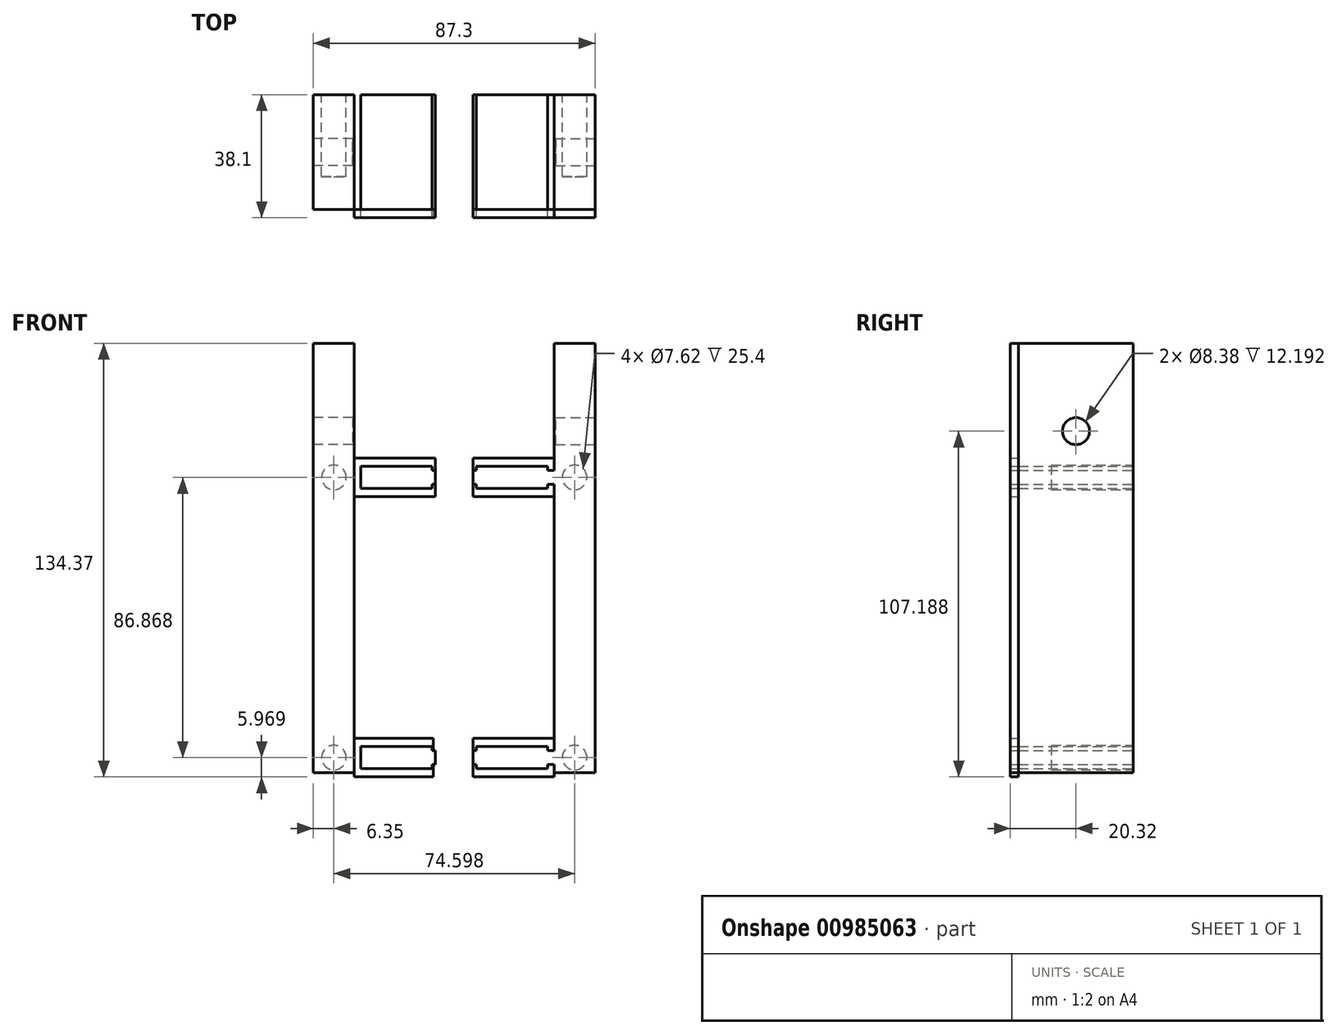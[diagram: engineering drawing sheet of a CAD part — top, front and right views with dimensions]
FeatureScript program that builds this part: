
annotation { "Feature Type Name" : "Feature", "Feature Type Description" : "" }
export const myFeature = defineFeature(function(context is Context, id is Id, definition is map)
    precondition{}
    {
        {
            var Q0;
            Q0=qCreatedBy(makeId("Front.planeOp"),FACE);
            var sketch = newSketch(context, id + "F0", { "sketchPlane" : qUnion([Q0])});
            skLineSegment(sketch, "E0.bottom", {"start": v(-12.7, 133.1) * mm, "end": v(0, 133.1) * mm});
            skLineSegment(sketch, "E0.top", {"start": v(-12.7, 0) * mm, "end": v(0, 0) * mm});
            skLineSegment(sketch, "E0.left", {"start": v(-12.7, 133.1) * mm, "end": v(-12.7, 0) * mm});
            skLineSegment(sketch, "E0.right", {"start": v(0, 133.1) * mm, "end": v(0, 0) * mm});
            skLineSegment(sketch, "E1.bottom", {"start": v(0, 6.86) * mm, "end": v(25.15, 6.86) * mm});
            skLineSegment(sketch, "E1.top", {"start": v(0, 2.54) * mm, "end": v(25.15, 2.54) * mm});
            skLineSegment(sketch, "E1.left", {"start": v(0, 6.86) * mm, "end": v(0, 2.54) * mm});
            skLineSegment(sketch, "E1.right", {"start": v(25.15, 6.86) * mm, "end": v(25.15, 2.54) * mm});
            skLineSegment(sketch, "E2.bottom", {"start": v(2.03, 8.13) * mm, "end": v(24.13, 8.13) * mm});
            skLineSegment(sketch, "E2.top", {"start": v(2.03, 1.27) * mm, "end": v(24.13, 1.27) * mm});
            skLineSegment(sketch, "E2.left", {"start": v(2.03, 8.13) * mm, "end": v(2.03, 1.27) * mm});
            skLineSegment(sketch, "E2.right", {"start": v(24.13, 8.13) * mm, "end": v(24.13, 1.27) * mm});
            skLineSegment(sketch, "E3.bottom", {"start": v(0, 93.73) * mm, "end": v(25.15, 93.73) * mm});
            skLineSegment(sketch, "E3.top", {"start": v(0, 89.4) * mm, "end": v(25.15, 89.4) * mm});
            skLineSegment(sketch, "E3.left", {"start": v(0, 93.73) * mm, "end": v(0, 89.4) * mm});
            skLineSegment(sketch, "E3.right", {"start": v(25.15, 93.73) * mm, "end": v(25.15, 89.4) * mm});
            skLineSegment(sketch, "E4.bottom", {"start": v(2.03, 95) * mm, "end": v(24.13, 95) * mm});
            skLineSegment(sketch, "E4.top", {"start": v(2.03, 88.14) * mm, "end": v(24.13, 88.14) * mm});
            skLineSegment(sketch, "E4.left", {"start": v(2.03, 95) * mm, "end": v(2.03, 88.14) * mm});
            skLineSegment(sketch, "E4.right", {"start": v(24.13, 95) * mm, "end": v(24.13, 88.14) * mm});
            skLineSegment(sketch, "E5", {"start": v(30.95, 107.36) * mm, "end": v(30.95, 0) * mm});
            skLineSegment(sketch, "E6.MirrorCS", {"start": v(59.87, 88.14) * mm, "end": v(37.77, 88.14) * mm});
            skLineSegment(sketch, "E7.MirrorCS", {"start": v(37.77, 95) * mm, "end": v(37.77, 88.14) * mm});
            skLineSegment(sketch, "E8.MirrorCS", {"start": v(61.9, 2.54) * mm, "end": v(36.75, 2.54) * mm});
            skLineSegment(sketch, "E9.MirrorCS", {"start": v(61.9, 6.86) * mm, "end": v(36.75, 6.86) * mm});
            skLineSegment(sketch, "E10.MirrorCS", {"start": v(61.9, 93.73) * mm, "end": v(61.9, 89.4) * mm});
            skLineSegment(sketch, "E11.MirrorCS", {"start": v(59.87, 95) * mm, "end": v(37.77, 95) * mm});
            skLineSegment(sketch, "E12.MirrorCS", {"start": v(59.87, 8.13) * mm, "end": v(37.77, 8.13) * mm});
            skLineSegment(sketch, "E13.MirrorCS", {"start": v(36.75, 6.86) * mm, "end": v(36.75, 2.54) * mm});
            skLineSegment(sketch, "E14.MirrorCS", {"start": v(37.77, 8.13) * mm, "end": v(37.77, 1.27) * mm});
            skLineSegment(sketch, "E15.MirrorCS", {"start": v(59.87, 1.27) * mm, "end": v(37.77, 1.27) * mm});
            skLineSegment(sketch, "E16.MirrorCS", {"start": v(36.75, 93.73) * mm, "end": v(36.75, 89.4) * mm});
            skLineSegment(sketch, "E17.MirrorCS", {"start": v(61.9, 89.4) * mm, "end": v(36.75, 89.4) * mm});
            skLineSegment(sketch, "E18.MirrorCS", {"start": v(59.87, 8.13) * mm, "end": v(59.87, 1.27) * mm});
            skLineSegment(sketch, "E19.MirrorCS", {"start": v(61.9, 6.86) * mm, "end": v(61.9, 2.54) * mm});
            skLineSegment(sketch, "E20.MirrorCS", {"start": v(61.9, 93.73) * mm, "end": v(36.75, 93.73) * mm});
            skLineSegment(sketch, "E21.MirrorCS", {"start": v(59.87, 95) * mm, "end": v(59.87, 88.14) * mm});
            skLineSegment(sketch, "E22.MirrorCS", {"start": v(74.6, 0) * mm, "end": v(61.9, 0) * mm});
            skLineSegment(sketch, "E23.MirrorCS", {"start": v(61.9, 133.1) * mm, "end": v(61.9, 0) * mm});
            skLineSegment(sketch, "E24.MirrorCS", {"start": v(74.6, 133.1) * mm, "end": v(61.9, 133.1) * mm});
            skLineSegment(sketch, "E25.MirrorCS", {"start": v(74.6, 133.1) * mm, "end": v(74.6, 0) * mm});
            skSolve(sketch);
        }
        {
            var Q0;
            {var subQ1=sQuery(id+"F0.wireOp",EDGE,"E0.bottom");Q0=makeQuery(id+"F0.imprint","IMPRINT",FACE,{"disambiguationData":[TD([[makeQuery(id+"F0.imprint","IMPRINT",EDGE,{"derivedFrom":subQ1}),-1.0]])]});}
            var Q1;
            {var subQ0=sQuery(id+"F0.wireOp",EDGE,"E2.left");var subQ1=sQuery(id+"F0.wireOp",EDGE,"E1.bottom");var subQ2=makeQuery(id+"F0.imprint","INTERSECT",VERTEX,{"derivedFrom":[subQ1,subQ0]});Q1=makeQuery(id+"F0.imprint","IMPRINT",FACE,{"disambiguationData":[TD([[makeQuery(id+"F0.imprint","IMPRINT",EDGE,{"disambiguationData":[TD([[subQ2,-1.0]])],"derivedFrom":subQ1}),-1.0]])]});}
            var Q2;
            {var subQ0=sQuery(id+"F0.wireOp",EDGE,"E1.left");Q2=makeQuery(id+"F0.imprint","IMPRINT",FACE,{"disambiguationData":[TD([[makeQuery(id+"F0.imprint","IMPRINT",EDGE,{"derivedFrom":subQ0}),1.0]])]});}
            var Q3;
            {var subQ5=sQuery(id+"F0.wireOp",EDGE,"E2.top");Q3=makeQuery(id+"F0.imprint","IMPRINT",FACE,{"disambiguationData":[TD([[makeQuery(id+"F0.imprint","IMPRINT",EDGE,{"derivedFrom":subQ5}),1.0]])]});}
            var Q4;
            {var subQ0=sQuery(id+"F0.wireOp",EDGE,"E1.right");Q4=makeQuery(id+"F0.imprint","IMPRINT",FACE,{"disambiguationData":[TD([[makeQuery(id+"F0.imprint","IMPRINT",EDGE,{"derivedFrom":subQ0}),-1.0]])]});}
            var Q5;
            {var subQ5=sQuery(id+"F0.wireOp",EDGE,"E2.bottom");Q5=makeQuery(id+"F0.imprint","IMPRINT",FACE,{"disambiguationData":[TD([[makeQuery(id+"F0.imprint","IMPRINT",EDGE,{"derivedFrom":subQ5}),-1.0]])]});}
            var Q6;
            {var subQ0=sQuery(id+"F0.wireOp",EDGE,"E4.left");var subQ1=sQuery(id+"F0.wireOp",EDGE,"E3.bottom");var subQ2=makeQuery(id+"F0.imprint","INTERSECT",VERTEX,{"derivedFrom":[subQ1,subQ0]});Q6=makeQuery(id+"F0.imprint","IMPRINT",FACE,{"disambiguationData":[TD([[makeQuery(id+"F0.imprint","IMPRINT",EDGE,{"disambiguationData":[TD([[subQ2,-1.0]])],"derivedFrom":subQ1}),-1.0]])]});}
            var Q7;
            {var subQ0=sQuery(id+"F0.wireOp",EDGE,"E3.left");Q7=makeQuery(id+"F0.imprint","IMPRINT",FACE,{"disambiguationData":[TD([[makeQuery(id+"F0.imprint","IMPRINT",EDGE,{"derivedFrom":subQ0}),1.0]])]});}
            var Q8;
            {var subQ5=sQuery(id+"F0.wireOp",EDGE,"E4.bottom");Q8=makeQuery(id+"F0.imprint","IMPRINT",FACE,{"disambiguationData":[TD([[makeQuery(id+"F0.imprint","IMPRINT",EDGE,{"derivedFrom":subQ5}),-1.0]])]});}
            var Q9;
            {var subQ0=sQuery(id+"F0.wireOp",EDGE,"E3.right");Q9=makeQuery(id+"F0.imprint","IMPRINT",FACE,{"disambiguationData":[TD([[makeQuery(id+"F0.imprint","IMPRINT",EDGE,{"derivedFrom":subQ0}),-1.0]])]});}
            var Q10;
            {var subQ5=sQuery(id+"F0.wireOp",EDGE,"E4.top");Q10=makeQuery(id+"F0.imprint","IMPRINT",FACE,{"disambiguationData":[TD([[makeQuery(id+"F0.imprint","IMPRINT",EDGE,{"derivedFrom":subQ5}),1.0]])]});}
            var Q11;
            {var subQ5=sQuery(id+"F0.wireOp",EDGE,"E22.MirrorCS");Q11=makeQuery(id+"F0.imprint","IMPRINT",FACE,{"disambiguationData":[TD([[makeQuery(id+"F0.imprint","IMPRINT",EDGE,{"derivedFrom":subQ5}),-1.0]])]});}
            var Q12;
            {var subQ5=sQuery(id+"F0.wireOp",EDGE,"E15.MirrorCS");Q12=makeQuery(id+"F0.imprint","IMPRINT",FACE,{"disambiguationData":[TD([[makeQuery(id+"F0.imprint","IMPRINT",EDGE,{"derivedFrom":subQ5}),-1.0]])]});}
            var Q13;
            {var subQ0=sQuery(id+"F0.wireOp",EDGE,"E18.MirrorCS");var subQ1=sQuery(id+"F0.wireOp",EDGE,"E8.MirrorCS");var subQ2=makeQuery(id+"F0.imprint","INTERSECT",VERTEX,{"derivedFrom":[subQ1,subQ0]});Q13=makeQuery(id+"F0.imprint","IMPRINT",FACE,{"disambiguationData":[TD([[makeQuery(id+"F0.imprint","IMPRINT",EDGE,{"disambiguationData":[TD([[subQ2,-1.0]])],"derivedFrom":subQ1}),-1.0]])]});}
            var Q14;
            {var subQ0=sQuery(id+"F0.wireOp",EDGE,"E13.MirrorCS");Q14=makeQuery(id+"F0.imprint","IMPRINT",FACE,{"disambiguationData":[TD([[makeQuery(id+"F0.imprint","IMPRINT",EDGE,{"derivedFrom":subQ0}),1.0]])]});}
            var Q15;
            {var subQ0=sQuery(id+"F0.wireOp",EDGE,"E23.MirrorCS");var subQ1=sQuery(id+"F0.wireOp",EDGE,"E8.MirrorCS");var subQ2=makeQuery(id+"F0.imprint","INTERSECT",VERTEX,{"derivedFrom":[subQ1,subQ0]});Q15=makeQuery(id+"F0.imprint","IMPRINT",FACE,{"disambiguationData":[TD([[makeQuery(id+"F0.imprint","IMPRINT",EDGE,{"disambiguationData":[TD([[subQ2,-1.0]])],"derivedFrom":subQ1}),-1.0]])]});}
            var Q16;
            {var subQ5=sQuery(id+"F0.wireOp",EDGE,"E12.MirrorCS");Q16=makeQuery(id+"F0.imprint","IMPRINT",FACE,{"disambiguationData":[TD([[makeQuery(id+"F0.imprint","IMPRINT",EDGE,{"derivedFrom":subQ5}),1.0]])]});}
            var Q17;
            {var subQ0=sQuery(id+"F0.wireOp",EDGE,"E6.MirrorCS");Q17=makeQuery(id+"F0.imprint","IMPRINT",FACE,{"disambiguationData":[TD([[makeQuery(id+"F0.imprint","IMPRINT",EDGE,{"derivedFrom":subQ0}),-1.0]])]});}
            var Q18;
            {var subQ0=sQuery(id+"F0.wireOp",EDGE,"E20.MirrorCS");var subQ1=sQuery(id+"F0.wireOp",EDGE,"E7.MirrorCS");var subQ2=makeQuery(id+"F0.imprint","INTERSECT",VERTEX,{"derivedFrom":[subQ1,subQ0]});Q18=makeQuery(id+"F0.imprint","IMPRINT",FACE,{"disambiguationData":[TD([[makeQuery(id+"F0.imprint","IMPRINT",EDGE,{"disambiguationData":[TD([[subQ2,-1.0]])],"derivedFrom":subQ1}),1.0]])]});}
            var Q19;
            {var subQ5=sQuery(id+"F0.wireOp",EDGE,"E16.MirrorCS");Q19=makeQuery(id+"F0.imprint","IMPRINT",FACE,{"disambiguationData":[TD([[makeQuery(id+"F0.imprint","IMPRINT",EDGE,{"derivedFrom":subQ5}),1.0]])]});}
            var Q20;
            {var subQ0=sQuery(id+"F0.wireOp",EDGE,"E23.MirrorCS");var subQ1=sQuery(id+"F0.wireOp",EDGE,"E17.MirrorCS");var subQ2=makeQuery(id+"F0.imprint","INTERSECT",VERTEX,{"derivedFrom":[subQ1,subQ0]});Q20=makeQuery(id+"F0.imprint","IMPRINT",FACE,{"disambiguationData":[TD([[makeQuery(id+"F0.imprint","IMPRINT",EDGE,{"disambiguationData":[TD([[subQ2,-1.0]])],"derivedFrom":subQ1}),-1.0]])]});}
            var Q21;
            {var subQ0=sQuery(id+"F0.wireOp",EDGE,"E11.MirrorCS");Q21=makeQuery(id+"F0.imprint","IMPRINT",FACE,{"disambiguationData":[TD([[makeQuery(id+"F0.imprint","IMPRINT",EDGE,{"derivedFrom":subQ0}),1.0]])]});}
            extrude(context, id + "F1", {"entities" : qUnion([Q0, Q1, Q2, Q3, Q4, Q5, Q6, Q7, Q8, Q9, Q10, Q11, Q12, Q13, Q14, Q15, Q16, Q17, Q18, Q19, Q20, Q21]), "depth" : 35.56 * mm, "offsetDistance" : 25.4 * mm});
        }
        {
            var Q0;
            Q0=makeQuery(id+"F1.opExtrude","CAP_FACE",FACE,{"disambiguationData":[OSD([sQuery(id+"F0.wireOp",EDGE,"E0.bottom"),sQuery(id+"F0.wireOp",EDGE,"E0.top"),sQuery(id+"F0.wireOp",EDGE,"E0.left"),sQuery(id+"F0.wireOp",EDGE,"E0.right"),sQuery(id+"F0.wireOp",EDGE,"E1.bottom"),sQuery(id+"F0.wireOp",EDGE,"E1.top"),sQuery(id+"F0.wireOp",EDGE,"E1.right"),sQuery(id+"F0.wireOp",EDGE,"E2.bottom"),sQuery(id+"F0.wireOp",EDGE,"E2.top"),sQuery(id+"F0.wireOp",EDGE,"E2.left"),sQuery(id+"F0.wireOp",EDGE,"E2.right"),sQuery(id+"F0.wireOp",EDGE,"E3.bottom"),sQuery(id+"F0.wireOp",EDGE,"E3.top"),sQuery(id+"F0.wireOp",EDGE,"E3.right"),sQuery(id+"F0.wireOp",EDGE,"E4.bottom"),sQuery(id+"F0.wireOp",EDGE,"E4.top"),sQuery(id+"F0.wireOp",EDGE,"E4.left"),sQuery(id+"F0.wireOp",EDGE,"E4.right")])],"isStart":false});
            var sketch = newSketch(context, id + "F2", { "sketchPlane" : qUnion([Q0])});
            skLineSegment(sketch, "E26.bottom", {"start": v(0, -1.27) * mm, "end": v(24.47, -1.27) * mm});
            skLineSegment(sketch, "E26.top", {"start": v(0, 10.67) * mm, "end": v(24.47, 10.67) * mm});
            skLineSegment(sketch, "E26.left", {"start": v(0, -1.27) * mm, "end": v(0, 10.67) * mm});
            skLineSegment(sketch, "E26.right", {"start": v(24.47, -1.27) * mm, "end": v(24.47, 10.67) * mm});
            skPoint(sketch, "E26.middle", {"position": v(12.24, 4.7) * mm});
            skPoint(sketch, "E26.middle.positionSnap0", {"position": v(25.15, 4.7) * mm});
            skPoint(sketch, "E26.centerSnap0", {"position": v(25.15, 4.7) * mm});
            skLineSegment(sketch, "E27.bottom", {"start": v(0, 85.6) * mm, "end": v(25.15, 85.6) * mm});
            skLineSegment(sketch, "E27.top", {"start": v(0, 97.54) * mm, "end": v(25.15, 97.54) * mm});
            skLineSegment(sketch, "E27.left", {"start": v(0, 85.6) * mm, "end": v(0, 97.54) * mm});
            skLineSegment(sketch, "E27.right", {"start": v(25.15, 85.6) * mm, "end": v(25.15, 97.54) * mm});
            skPoint(sketch, "E27.middle", {"position": v(12.57, 91.57) * mm});
            skPoint(sketch, "E27.middle.positionSnap0", {"position": v(25.15, 91.57) * mm});
            skPoint(sketch, "E27.centerSnap0", {"position": v(25.15, 91.57) * mm});
            skSolve(sketch);
        }
        {
            var Q0;
            Q0=makeQuery(id+"F1.opExtrude","CAP_FACE",FACE,{"disambiguationData":[OSD([sQuery(id+"F0.wireOp",EDGE,"E6.MirrorCS"),sQuery(id+"F0.wireOp",EDGE,"E7.MirrorCS"),sQuery(id+"F0.wireOp",EDGE,"E8.MirrorCS"),sQuery(id+"F0.wireOp",EDGE,"E9.MirrorCS"),sQuery(id+"F0.wireOp",EDGE,"E11.MirrorCS"),sQuery(id+"F0.wireOp",EDGE,"E12.MirrorCS"),sQuery(id+"F0.wireOp",EDGE,"E13.MirrorCS"),sQuery(id+"F0.wireOp",EDGE,"E14.MirrorCS"),sQuery(id+"F0.wireOp",EDGE,"E15.MirrorCS"),sQuery(id+"F0.wireOp",EDGE,"E16.MirrorCS"),sQuery(id+"F0.wireOp",EDGE,"E17.MirrorCS"),sQuery(id+"F0.wireOp",EDGE,"E18.MirrorCS"),sQuery(id+"F0.wireOp",EDGE,"E20.MirrorCS"),sQuery(id+"F0.wireOp",EDGE,"E21.MirrorCS"),sQuery(id+"F0.wireOp",EDGE,"E22.MirrorCS"),sQuery(id+"F0.wireOp",EDGE,"E23.MirrorCS"),sQuery(id+"F0.wireOp",EDGE,"E24.MirrorCS"),sQuery(id+"F0.wireOp",EDGE,"E25.MirrorCS")])],"isStart":false});
            var sketch = newSketch(context, id + "F3", { "sketchPlane" : qUnion([Q0])});
            skLineSegment(sketch, "E28.bottom", {"start": v(36.75, 85.6) * mm, "end": v(61.9, 85.6) * mm});
            skLineSegment(sketch, "E28.top", {"start": v(36.75, 97.54) * mm, "end": v(61.9, 97.54) * mm});
            skLineSegment(sketch, "E28.left", {"start": v(36.75, 85.6) * mm, "end": v(36.75, 97.54) * mm});
            skLineSegment(sketch, "E28.right", {"start": v(61.9, 85.6) * mm, "end": v(61.9, 97.54) * mm});
            skPoint(sketch, "E28.middle", {"position": v(49.33, 91.57) * mm});
            skPoint(sketch, "E28.middle.positionSnap0", {"position": v(36.75, 91.57) * mm});
            skPoint(sketch, "E28.cornerSnap0", {"position": v(36.75, 91.57) * mm});
            skPoint(sketch, "E28.centerSnap0", {"position": v(36.75, 91.57) * mm});
            skLineSegment(sketch, "E29.bottom", {"start": v(36.75, -1.27) * mm, "end": v(61.9, -1.27) * mm});
            skLineSegment(sketch, "E29.top", {"start": v(36.75, 10.67) * mm, "end": v(61.9, 10.67) * mm});
            skLineSegment(sketch, "E29.left", {"start": v(36.75, -1.27) * mm, "end": v(36.75, 10.67) * mm});
            skLineSegment(sketch, "E29.right", {"start": v(61.9, -1.27) * mm, "end": v(61.9, 10.67) * mm});
            skPoint(sketch, "E29.middle", {"position": v(49.33, 4.7) * mm});
            skPoint(sketch, "E29.middle.positionSnap0", {"position": v(36.75, 4.7) * mm});
            skPoint(sketch, "E29.centerSnap0", {"position": v(36.75, 4.7) * mm});
            skSolve(sketch);
        }
        {
            var Q0;
            {var subQ8=sQuery(id+"F3.wireOp",EDGE,"E28.bottom");Q0=makeQuery(id+"F3.imprint","IMPRINT",FACE,{"disambiguationData":[TD([[makeQuery(id+"F3.imprint","IMPRINT",EDGE,{"derivedFrom":subQ8}),1.0]])]});}
            var Q1;
            {var subQ6=sQuery(id+"F3.wireOp",EDGE,"E28.top");Q1=makeQuery(id+"F3.imprint","IMPRINT",FACE,{"disambiguationData":[TD([[makeQuery(id+"F3.imprint","IMPRINT",EDGE,{"derivedFrom":subQ6}),-1.0]])]});}
            var Q2;
            {var subQ2=sQuery(id+"F2.wireOp",EDGE,"E27.top");Q2=makeQuery(id+"F2.imprint","IMPRINT",FACE,{"disambiguationData":[TD([[makeQuery(id+"F2.imprint","IMPRINT",EDGE,{"derivedFrom":subQ2}),-1.0]])]});}
            var Q3;
            {var subQ10=sQuery(id+"F2.wireOp",EDGE,"E27.bottom");Q3=makeQuery(id+"F2.imprint","IMPRINT",FACE,{"disambiguationData":[TD([[makeQuery(id+"F2.imprint","IMPRINT",EDGE,{"derivedFrom":subQ10}),1.0]])]});}
            var Q4;
            {var subQ10=sQuery(id+"F3.wireOp",EDGE,"E29.top");Q4=makeQuery(id+"F3.imprint","IMPRINT",FACE,{"disambiguationData":[TD([[makeQuery(id+"F3.imprint","IMPRINT",EDGE,{"derivedFrom":subQ10}),-1.0]])]});}
            var Q5;
            {var subQ11=sQuery(id+"F3.wireOp",EDGE,"E29.bottom");Q5=makeQuery(id+"F3.imprint","IMPRINT",FACE,{"disambiguationData":[TD([[makeQuery(id+"F3.imprint","IMPRINT",EDGE,{"derivedFrom":subQ11}),1.0]])]});}
            var Q6;
            {var subQ7=sQuery(id+"F2.wireOp",EDGE,"E26.top");Q6=makeQuery(id+"F2.imprint","IMPRINT",FACE,{"disambiguationData":[TD([[makeQuery(id+"F2.imprint","IMPRINT",EDGE,{"derivedFrom":subQ7}),-1.0]])]});}
            var Q7;
            {var subQ1=sQuery(id+"F2.wireOp",EDGE,"E26.bottom");Q7=makeQuery(id+"F2.imprint","IMPRINT",FACE,{"disambiguationData":[TD([[makeQuery(id+"F2.imprint","IMPRINT",EDGE,{"derivedFrom":subQ1}),1.0]])]});}
            extrude(context, id + "F4", {"entities" : qUnion([Q0, Q1, Q2, Q3, Q4, Q5, Q6, Q7]), "depth" : 2.54 * mm, "offsetDistance" : 25.4 * mm});
        }
        {
            var Q0;
            Q0=makeQuery(id+"F1.opExtrude","SWEPT_FACE",FACE,{"disambiguationData":[OSD([sQuery(id+"F0.wireOp",EDGE,"E0.left")])]});
            var sketch = newSketch(context, id + "F5", { "sketchPlane" : qUnion([Q0])});
            skLineSegment(sketch, "E30", {"start": v(0, 0) * mm, "end": v(0, 105.92) * mm});
            skLineSegment(sketch, "E31", {"start": v(0, 0) * mm, "end": v(0, 105.33) * mm});
            skPoint(sketch, "E32.middle", {"position": v(17.78, 105.92) * mm});
            skLineSegment(sketch, "E33.right", {"start": v(35.56, 126.24) * mm, "end": v(35.56, 85.6) * mm});
            skCircle(sketch, "E34", {"center": v(17.78, 105.92) * mm, "radius": 4.2 * mm});
            skSolve(sketch);
        }
        {
            var Q0;
            Q0=makeQuery(id+"F5.imprint","IMPRINT",FACE,{"disambiguationData":[TD([[makeQuery(id+"F5.imprint","IMPRINT",EDGE,{"derivedFrom":sQuery(id+"F5.wireOp",EDGE,"E34")}),1.0]])]});
            extrude(context, id + "F6", {"entities" : qUnion([Q0]), "operationType" : NewBodyOperationType.REMOVE, "oppositeDirection" : true, "depth" : 12.2 * mm, "offsetDistance" : 25.4 * mm});
        }
        {
            var Q0;
            Q0=makeQuery(id+"F1.opExtrude","SWEPT_FACE",FACE,{"disambiguationData":[OSD([sQuery(id+"F0.wireOp",EDGE,"E25.MirrorCS")])]});
            var sketch = newSketch(context, id + "F7", { "sketchPlane" : qUnion([Q0])});
            skCircle(sketch, "E35", {"center": v(-17.78, 105.92) * mm, "radius": 4.2 * mm});
            skSolve(sketch);
        }
        {
            var Q0;
            Q0=makeQuery(id+"F7.imprint","IMPRINT",FACE,{"disambiguationData":[TD([[makeQuery(id+"F7.imprint","IMPRINT",EDGE,{"derivedFrom":sQuery(id+"F7.wireOp",EDGE,"E35")}),1.0]])]});
            extrude(context, id + "F8", {"entities" : qUnion([Q0]), "operationType" : NewBodyOperationType.REMOVE, "oppositeDirection" : true, "depth" : 12.2 * mm, "offsetDistance" : 25.4 * mm});
        }
        {
            var Q0;
            Q0=makeQuery(id+"F1.opExtrude","CAP_FACE",FACE,{"disambiguationData":[OSD([sQuery(id+"F0.wireOp",EDGE,"E6.MirrorCS"),sQuery(id+"F0.wireOp",EDGE,"E7.MirrorCS"),sQuery(id+"F0.wireOp",EDGE,"E8.MirrorCS"),sQuery(id+"F0.wireOp",EDGE,"E9.MirrorCS"),sQuery(id+"F0.wireOp",EDGE,"E11.MirrorCS"),sQuery(id+"F0.wireOp",EDGE,"E12.MirrorCS"),sQuery(id+"F0.wireOp",EDGE,"E13.MirrorCS"),sQuery(id+"F0.wireOp",EDGE,"E14.MirrorCS"),sQuery(id+"F0.wireOp",EDGE,"E15.MirrorCS"),sQuery(id+"F0.wireOp",EDGE,"E16.MirrorCS"),sQuery(id+"F0.wireOp",EDGE,"E17.MirrorCS"),sQuery(id+"F0.wireOp",EDGE,"E18.MirrorCS"),sQuery(id+"F0.wireOp",EDGE,"E20.MirrorCS"),sQuery(id+"F0.wireOp",EDGE,"E21.MirrorCS"),sQuery(id+"F0.wireOp",EDGE,"E22.MirrorCS"),sQuery(id+"F0.wireOp",EDGE,"E23.MirrorCS"),sQuery(id+"F0.wireOp",EDGE,"E24.MirrorCS"),sQuery(id+"F0.wireOp",EDGE,"E25.MirrorCS")])],"isStart":true});
            var sketch = newSketch(context, id + "F9", { "sketchPlane" : qUnion([Q0])});
            skCircle(sketch, "E36", {"center": v(-68.25, 91.57) * mm, "radius": 3.81 * mm});
            skCircle(sketch, "E37", {"center": v(-68.25, 4.7) * mm, "radius": 3.81 * mm});
            skSolve(sketch);
        }
        {
            var Q0;
            Q0=makeQuery(id+"F1.opExtrude","CAP_FACE",FACE,{"disambiguationData":[OSD([sQuery(id+"F0.wireOp",EDGE,"E0.bottom"),sQuery(id+"F0.wireOp",EDGE,"E0.top"),sQuery(id+"F0.wireOp",EDGE,"E0.left"),sQuery(id+"F0.wireOp",EDGE,"E0.right"),sQuery(id+"F0.wireOp",EDGE,"E1.bottom"),sQuery(id+"F0.wireOp",EDGE,"E1.top"),sQuery(id+"F0.wireOp",EDGE,"E1.right"),sQuery(id+"F0.wireOp",EDGE,"E2.bottom"),sQuery(id+"F0.wireOp",EDGE,"E2.top"),sQuery(id+"F0.wireOp",EDGE,"E2.left"),sQuery(id+"F0.wireOp",EDGE,"E2.right"),sQuery(id+"F0.wireOp",EDGE,"E3.bottom"),sQuery(id+"F0.wireOp",EDGE,"E3.top"),sQuery(id+"F0.wireOp",EDGE,"E3.right"),sQuery(id+"F0.wireOp",EDGE,"E4.bottom"),sQuery(id+"F0.wireOp",EDGE,"E4.top"),sQuery(id+"F0.wireOp",EDGE,"E4.left"),sQuery(id+"F0.wireOp",EDGE,"E4.right")])],"isStart":true});
            var sketch = newSketch(context, id + "F10", { "sketchPlane" : qUnion([Q0])});
            skCircle(sketch, "E38", {"center": v(6.35, 4.7) * mm, "radius": 3.81 * mm});
            skCircle(sketch, "E39", {"center": v(6.35, 91.57) * mm, "radius": 3.81 * mm});
            skSolve(sketch);
        }
        {
            var Q0;
            Q0=makeQuery(id+"F10.imprint","IMPRINT",FACE,{"disambiguationData":[TD([[makeQuery(id+"F10.imprint","IMPRINT",EDGE,{"derivedFrom":sQuery(id+"F10.wireOp",EDGE,"E39")}),1.0]])]});
            var Q1;
            Q1=makeQuery(id+"F10.imprint","IMPRINT",FACE,{"disambiguationData":[TD([[makeQuery(id+"F10.imprint","IMPRINT",EDGE,{"derivedFrom":sQuery(id+"F10.wireOp",EDGE,"E38")}),1.0]])]});
            extrude(context, id + "F11", {"entities" : qUnion([Q0, Q1]), "operationType" : NewBodyOperationType.REMOVE, "oppositeDirection" : true, "depth" : 25.4 * mm, "offsetDistance" : 25.4 * mm});
        }
        {
            var Q0;
            Q0=makeQuery(id+"F9.imprint","IMPRINT",FACE,{"disambiguationData":[TD([[makeQuery(id+"F9.imprint","IMPRINT",EDGE,{"derivedFrom":sQuery(id+"F9.wireOp",EDGE,"E36")}),1.0]])]});
            var Q1;
            Q1=makeQuery(id+"F9.imprint","IMPRINT",FACE,{"disambiguationData":[TD([[makeQuery(id+"F9.imprint","IMPRINT",EDGE,{"derivedFrom":sQuery(id+"F9.wireOp",EDGE,"E37")}),1.0]])]});
            extrude(context, id + "F12", {"entities" : qUnion([Q0, Q1]), "operationType" : NewBodyOperationType.REMOVE, "oppositeDirection" : true, "depth" : 25.4 * mm, "offsetDistance" : 25.4 * mm});
        }
        {
            var Q0;
            Q0=makeQuery(id+"F1.opExtrude","CAP_FACE",FACE,{"disambiguationData":[OSD([sQuery(id+"F0.wireOp",EDGE,"E0.bottom"),sQuery(id+"F0.wireOp",EDGE,"E0.top"),sQuery(id+"F0.wireOp",EDGE,"E0.left"),sQuery(id+"F0.wireOp",EDGE,"E0.right"),sQuery(id+"F0.wireOp",EDGE,"E1.bottom"),sQuery(id+"F0.wireOp",EDGE,"E1.top"),sQuery(id+"F0.wireOp",EDGE,"E1.right"),sQuery(id+"F0.wireOp",EDGE,"E2.bottom"),sQuery(id+"F0.wireOp",EDGE,"E2.top"),sQuery(id+"F0.wireOp",EDGE,"E2.left"),sQuery(id+"F0.wireOp",EDGE,"E2.right"),sQuery(id+"F0.wireOp",EDGE,"E3.bottom"),sQuery(id+"F0.wireOp",EDGE,"E3.top"),sQuery(id+"F0.wireOp",EDGE,"E3.right"),sQuery(id+"F0.wireOp",EDGE,"E4.bottom"),sQuery(id+"F0.wireOp",EDGE,"E4.top"),sQuery(id+"F0.wireOp",EDGE,"E4.left"),sQuery(id+"F0.wireOp",EDGE,"E4.right")])],"isStart":false});
            var Q1;
            Q1=makeQuery(id+"F1.opExtrude","CAP_FACE",FACE,{"disambiguationData":[OSD([sQuery(id+"F0.wireOp",EDGE,"E6.MirrorCS"),sQuery(id+"F0.wireOp",EDGE,"E7.MirrorCS"),sQuery(id+"F0.wireOp",EDGE,"E8.MirrorCS"),sQuery(id+"F0.wireOp",EDGE,"E9.MirrorCS"),sQuery(id+"F0.wireOp",EDGE,"E11.MirrorCS"),sQuery(id+"F0.wireOp",EDGE,"E12.MirrorCS"),sQuery(id+"F0.wireOp",EDGE,"E13.MirrorCS"),sQuery(id+"F0.wireOp",EDGE,"E14.MirrorCS"),sQuery(id+"F0.wireOp",EDGE,"E15.MirrorCS"),sQuery(id+"F0.wireOp",EDGE,"E16.MirrorCS"),sQuery(id+"F0.wireOp",EDGE,"E17.MirrorCS"),sQuery(id+"F0.wireOp",EDGE,"E18.MirrorCS"),sQuery(id+"F0.wireOp",EDGE,"E20.MirrorCS"),sQuery(id+"F0.wireOp",EDGE,"E21.MirrorCS"),sQuery(id+"F0.wireOp",EDGE,"E22.MirrorCS"),sQuery(id+"F0.wireOp",EDGE,"E23.MirrorCS"),sQuery(id+"F0.wireOp",EDGE,"E24.MirrorCS"),sQuery(id+"F0.wireOp",EDGE,"E25.MirrorCS")])],"isStart":false});
            extrude(context, id + "F13", {"entities" : qUnion([Q0, Q1]), "depth" : 2.54 * mm, "offsetDistance" : 25.4 * mm});
        }
    });
